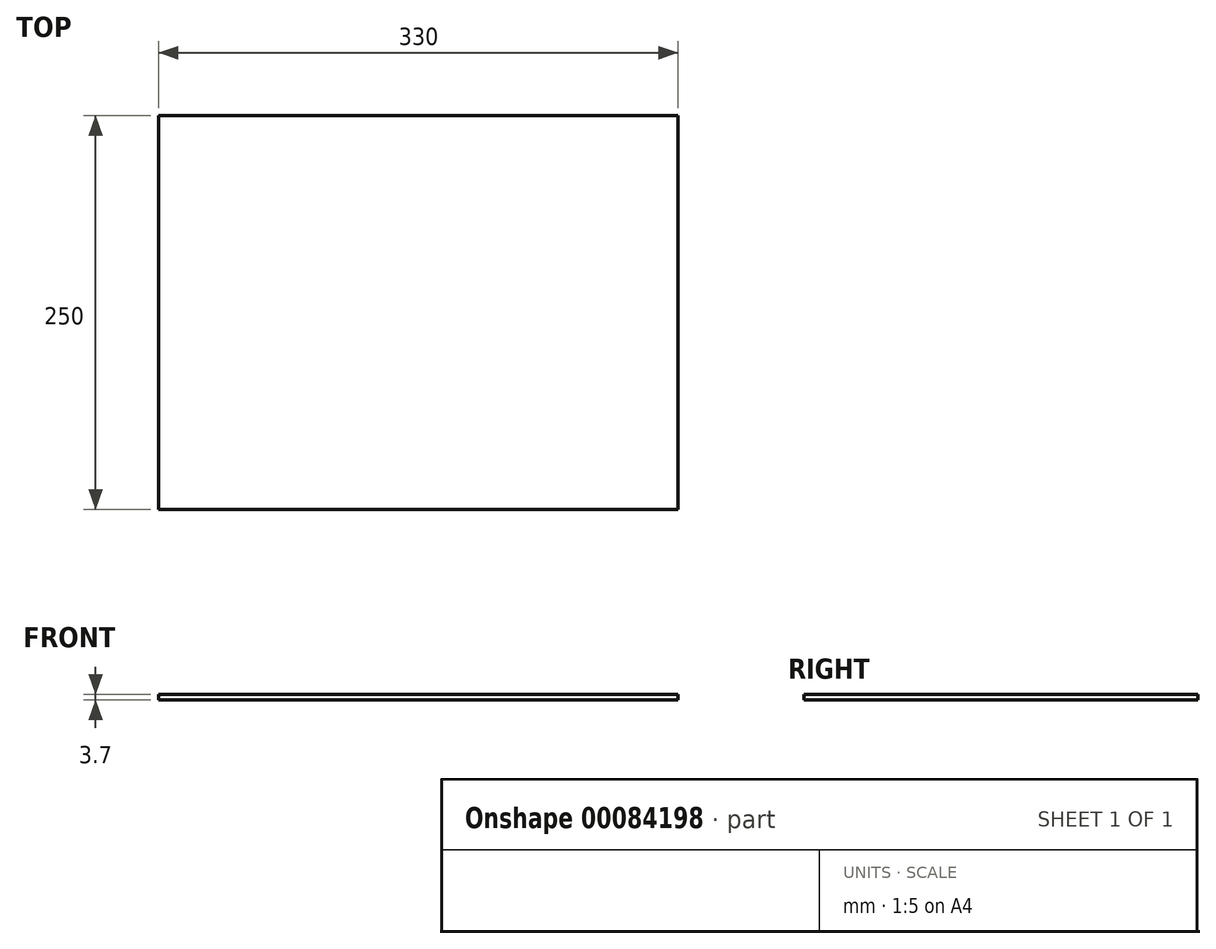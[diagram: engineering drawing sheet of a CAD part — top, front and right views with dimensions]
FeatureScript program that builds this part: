
annotation { "Feature Type Name" : "Feature", "Feature Type Description" : "" }
export const myFeature = defineFeature(function(context is Context, id is Id, definition is map)
    precondition{}
    {
        {
            var Q0;
            Q0=qCreatedBy(makeId("Top.planeOp"),FACE);
            var sketch = newSketch(context, id + "F0", { "sketchPlane" : qUnion([Q0])});
            skLineSegment(sketch, "E0.bottom", {"start": v(0, 250) * mm, "end": v(330, 250) * mm});
            skLineSegment(sketch, "E0.top", {"start": v(0, 0) * mm, "end": v(330, 0) * mm});
            skLineSegment(sketch, "E0.left", {"start": v(0, 250) * mm, "end": v(0, 0) * mm});
            skLineSegment(sketch, "E0.right", {"start": v(330, 250) * mm, "end": v(330, 0) * mm});
            skSolve(sketch);
        }
        {
            var Q0;
            Q0 = qSketchRegion(id + "F0", true);
            extrude(context, id + "F1", {"entities" : qUnion([Q0]), "depth" : 3.7 * mm});
        }
    });
